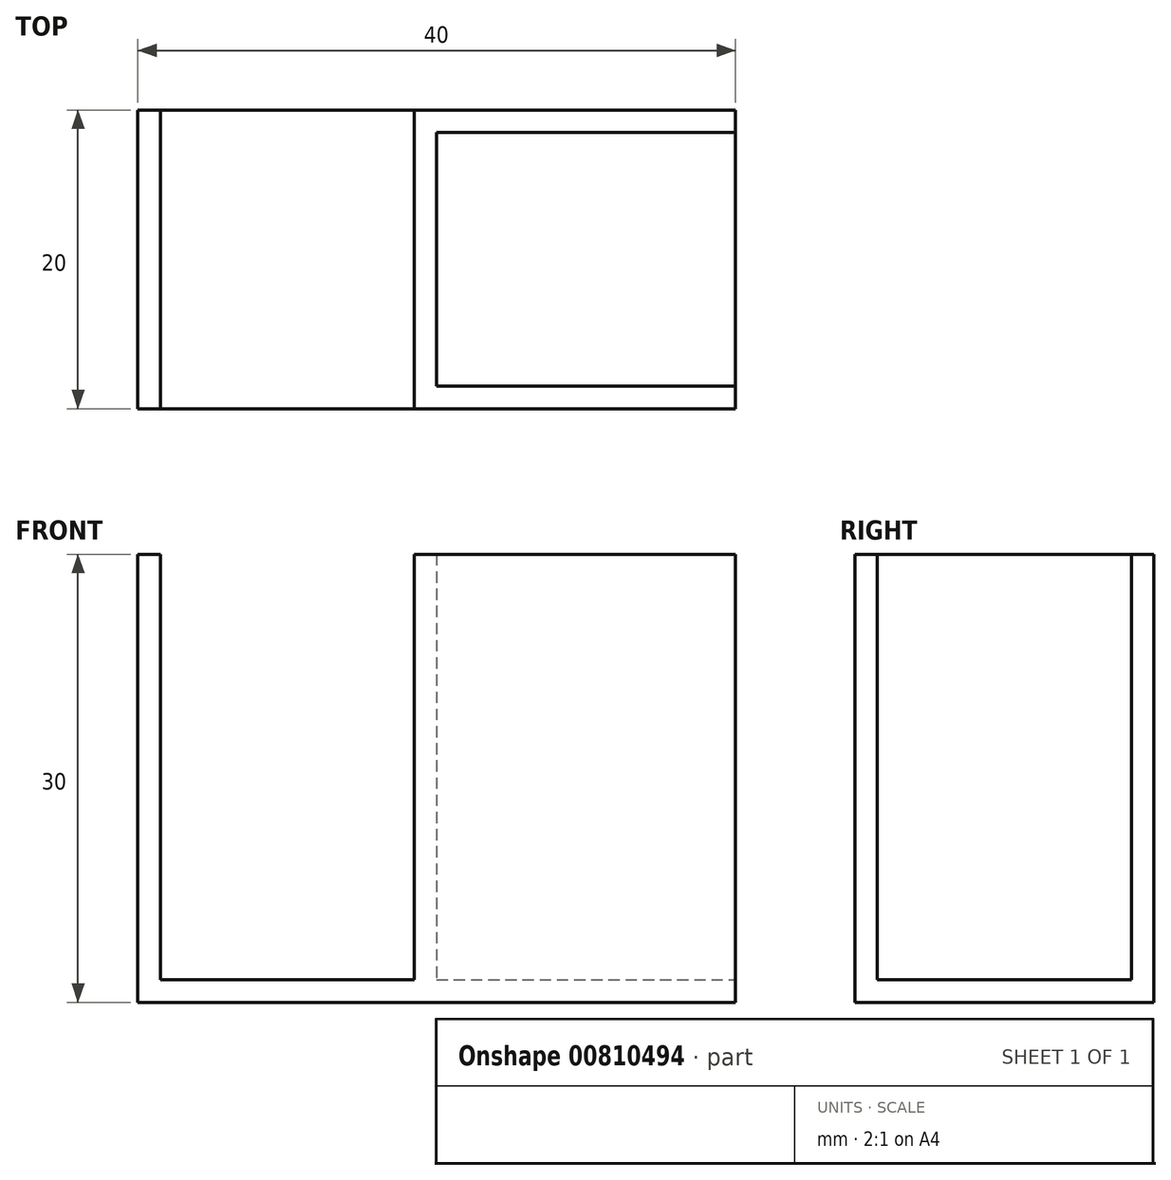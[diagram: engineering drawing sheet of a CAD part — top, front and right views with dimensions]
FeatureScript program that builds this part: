
annotation { "Feature Type Name" : "Feature", "Feature Type Description" : "" }
export const myFeature = defineFeature(function(context is Context, id is Id, definition is map)
    precondition{}
    {
        {
            var Q0;
            Q0=qCreatedBy(makeId("Front.planeOp"),FACE);
            var sketch = newSketch(context, id + "F0", { "sketchPlane" : qUnion([Q0])});
            skLineSegment(sketch, "E0.bottom", {"start": v(-20, 30) * mm, "end": v(-18.5, 30) * mm});
            skLineSegment(sketch, "E0.top", {"start": v(-20, 0) * mm, "end": v(0, 0) * mm});
            skLineSegment(sketch, "E0.left", {"start": v(-20, 30) * mm, "end": v(-20, 0) * mm});
            skLineSegment(sketch, "E0.right", {"start": v(0, 30) * mm, "end": v(0, 0) * mm});
            skLineSegment(sketch, "E1.top", {"start": v(-18.5, 1.5) * mm, "end": v(-1.5, 1.5) * mm});
            skLineSegment(sketch, "E1.left", {"start": v(-18.5, 30) * mm, "end": v(-18.5, 1.5) * mm});
            skLineSegment(sketch, "E1.right", {"start": v(-1.5, 30) * mm, "end": v(-1.5, 1.5) * mm});
            skLineSegment(sketch, "E2.trimOffspring", {"start": v(-1.5, 30) * mm, "end": v(0, 30) * mm});
            skLineSegment(sketch, "E3.bottom", {"start": v(0, 30) * mm, "end": v(20, 30) * mm});
            skLineSegment(sketch, "E3.top", {"start": v(0, 0) * mm, "end": v(20, 0) * mm});
            skLineSegment(sketch, "E3.right", {"start": v(20, 30) * mm, "end": v(20, 0) * mm});
            skSolve(sketch);
        }
        {
            var Q0;
            Q0 = qSketchRegion(id + "F0", true);
            extrude(context, id + "F1", {"entities" : qUnion([Q0]), "depth" : 20 * mm, "offsetDistance" : 25 * mm});
        }
        {
            var Q0;
            Q0=qCreatedBy(makeId("Right.planeOp"),FACE);
            cPlane(context, id + "F2", {"entities" : qUnion([Q0]), "cplaneType" : CPlaneType.OFFSET, "offset" : 30 * mm, "width" : 150 * mm, "height" : 150 * mm});
        }
        {
            var Q0;
            Q0=qCreatedBy(id+"F2.planeOp",FACE);
            var sketch = newSketch(context, id + "F3", { "sketchPlane" : qUnion([Q0])});
            skPoint(sketch, "E4.oppositeSnap0", {"position": v(-18.5, 30) * mm});
            skLineSegment(sketch, "E4.top", {"start": v(-1.5, 1.5) * mm, "end": v(-18.5, 1.5) * mm});
            skLineSegment(sketch, "E4.left", {"start": v(-1.5, 30) * mm, "end": v(-1.5, 1.5) * mm});
            skLineSegment(sketch, "E4.right", {"start": v(-18.5, 30) * mm, "end": v(-18.5, 1.5) * mm});
            skPoint(sketch, "E5.end.orphan", {"position": v(-17.4, 0) * mm});
            skLineSegment(sketch, "E6", {"start": v(-18.5, 30) * mm, "end": v(-1.5, 30) * mm});
            skSolve(sketch);
        }
        {
            var Q0;
            Q0 = qSketchRegion(id + "F3", true);
            extrude(context, id + "F4", {"entities" : qUnion([Q0]), "operationType" : NewBodyOperationType.REMOVE, "oppositeDirection" : true, "depth" : 30 * mm, "offsetDistance" : 25 * mm});
        }
    });
